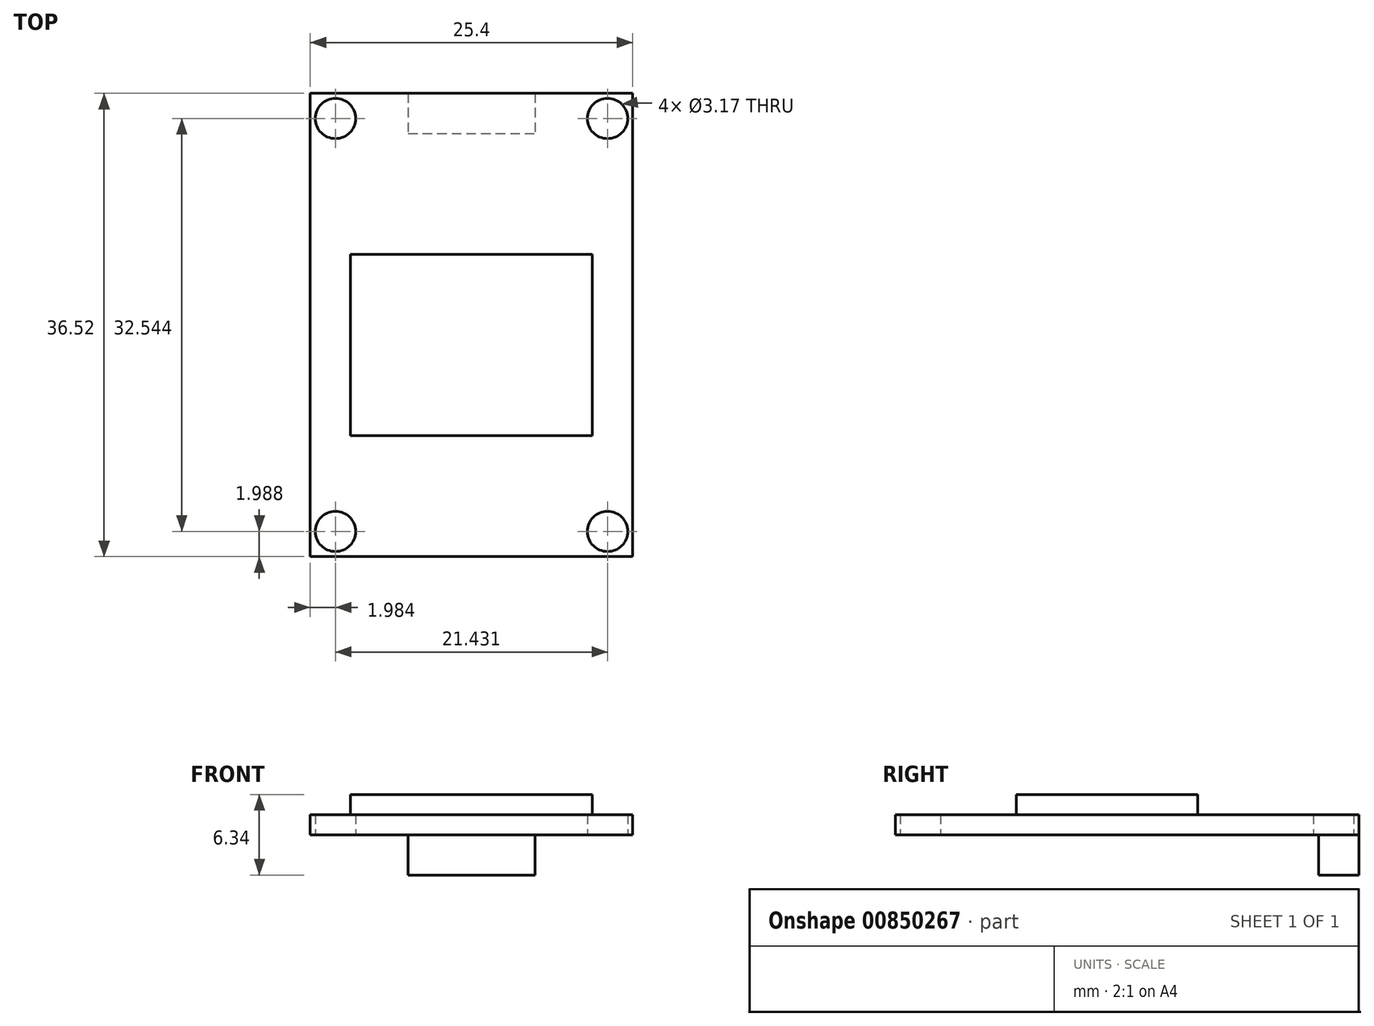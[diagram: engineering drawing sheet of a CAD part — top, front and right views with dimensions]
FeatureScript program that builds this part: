
annotation { "Feature Type Name" : "Feature", "Feature Type Description" : "" }
export const myFeature = defineFeature(function(context is Context, id is Id, definition is map)
    precondition{}
    {
        {
            var Q0;
            Q0=qCreatedBy(makeId("Top.planeOp"),FACE);
            var sketch = newSketch(context, id + "F0", { "sketchPlane" : qUnion([Q0])});
            skLineSegment(sketch, "E0.bottom", {"start": v(12.7, 18.26) * mm, "end": v(-12.7, 18.26) * mm});
            skLineSegment(sketch, "E0.top", {"start": v(12.7, -18.26) * mm, "end": v(-12.7, -18.26) * mm});
            skLineSegment(sketch, "E0.left", {"start": v(12.7, 18.26) * mm, "end": v(12.7, -18.26) * mm});
            skLineSegment(sketch, "E0.right", {"start": v(-12.7, 18.26) * mm, "end": v(-12.7, -18.26) * mm});
            skPoint(sketch, "E0.middle", {"position": v(0, 0) * mm});
            skCircle(sketch, "E1", {"center": v(-10.72, 16.27) * mm, "radius": 1.59 * mm});
            skCircle(sketch, "E2", {"center": v(10.72, 16.27) * mm, "radius": 1.59 * mm});
            skCircle(sketch, "E3", {"center": v(-10.72, -16.27) * mm, "radius": 1.59 * mm});
            skCircle(sketch, "E4", {"center": v(10.72, -16.27) * mm, "radius": 1.59 * mm});
            skLineSegment(sketch, "E5", {"start": v(-10.72, -16.27) * mm, "end": v(-10.72, 16.27) * mm, "construction": true});
            skLineSegment(sketch, "E6", {"start": v(-10.72, 16.27) * mm, "end": v(10.72, 16.27) * mm, "construction": true});
            skLineSegment(sketch, "E7", {"start": v(10.72, -16.27) * mm, "end": v(10.72, 16.27) * mm, "construction": true});
            skLineSegment(sketch, "E8", {"start": v(10.72, -16.27) * mm, "end": v(-10.72, -16.27) * mm, "construction": true});
            skSolve(sketch);
        }
        {
            var Q0;
            Q0=makeQuery(id+"F0.imprint","IMPRINT",FACE,{"disambiguationData":[TD([[makeQuery(id+"F0.imprint","IMPRINT",EDGE,{"derivedFrom":sQuery(id+"F0.wireOp",EDGE,"E0.bottom")}),1.0]])]});
            extrude(context, id + "F1", {"entities" : qUnion([Q0]), "depth" : 1.59 * mm, "offsetDistance" : 25.4 * mm});
        }
        {
            var Q0;
            Q0=makeQuery(id+"F1.opExtrude","CAP_FACE",FACE,{"disambiguationData":[OSD([sQuery(id+"F0.wireOp",EDGE,"E0.bottom"),sQuery(id+"F0.wireOp",EDGE,"E0.top"),sQuery(id+"F0.wireOp",EDGE,"E0.left"),sQuery(id+"F0.wireOp",EDGE,"E0.right"),sQuery(id+"F0.wireOp",EDGE,"E1"),sQuery(id+"F0.wireOp",EDGE,"E2"),sQuery(id+"F0.wireOp",EDGE,"E3"),sQuery(id+"F0.wireOp",EDGE,"E4")])],"isStart":false});
            var sketch = newSketch(context, id + "F2", { "sketchPlane" : qUnion([Q0])});
            skLineSegment(sketch, "E9.bottom", {"start": v(9.53, 5.56) * mm, "end": v(-9.53, 5.56) * mm});
            skLineSegment(sketch, "E9.top", {"start": v(9.53, -8.73) * mm, "end": v(-9.53, -8.73) * mm});
            skLineSegment(sketch, "E9.left", {"start": v(9.53, 5.56) * mm, "end": v(9.53, -8.73) * mm});
            skLineSegment(sketch, "E9.right", {"start": v(-9.53, 5.56) * mm, "end": v(-9.53, -8.73) * mm});
            skPoint(sketch, "E9.middle", {"position": v(0, -1.59) * mm});
            skSolve(sketch);
        }
        {
            var Q0;
            Q0=makeQuery(id+"F2.imprint","IMPRINT",FACE,{"disambiguationData":[TD([[makeQuery(id+"F2.imprint","IMPRINT",EDGE,{"derivedFrom":sQuery(id+"F2.wireOp",EDGE,"E9.bottom")}),1.0]])]});
            extrude(context, id + "F3", {"entities" : qUnion([Q0]), "operationType" : NewBodyOperationType.ADD, "depth" : 1.59 * mm, "offsetDistance" : 25.4 * mm});
        }
        {
            var Q0;
            Q0=makeQuery(id+"F1.opExtrude","CAP_FACE",FACE,{"disambiguationData":[OSD([sQuery(id+"F0.wireOp",EDGE,"E0.bottom"),sQuery(id+"F0.wireOp",EDGE,"E0.top"),sQuery(id+"F0.wireOp",EDGE,"E0.left"),sQuery(id+"F0.wireOp",EDGE,"E0.right"),sQuery(id+"F0.wireOp",EDGE,"E1"),sQuery(id+"F0.wireOp",EDGE,"E2"),sQuery(id+"F0.wireOp",EDGE,"E3"),sQuery(id+"F0.wireOp",EDGE,"E4")])],"isStart":true});
            var sketch = newSketch(context, id + "F4", { "sketchPlane" : qUnion([Q0])});
            skLineSegment(sketch, "E10.bottom", {"start": v(-5, -18.26) * mm, "end": v(5, -18.26) * mm});
            skLineSegment(sketch, "E10.top", {"start": v(-5, -15.08) * mm, "end": v(5, -15.08) * mm});
            skLineSegment(sketch, "E10.left", {"start": v(-5, -18.26) * mm, "end": v(-5, -15.08) * mm});
            skLineSegment(sketch, "E10.right", {"start": v(5, -18.26) * mm, "end": v(5, -15.08) * mm});
            skPoint(sketch, "E10.middle", {"position": v(0, -16.67) * mm});
            skSolve(sketch);
        }
        {
            var Q0;
            Q0=makeQuery(id+"F4.imprint","IMPRINT",FACE,{"disambiguationData":[TD([[makeQuery(id+"F4.imprint","IMPRINT",EDGE,{"derivedFrom":sQuery(id+"F4.wireOp",EDGE,"E10.bottom")}),-1.0]])]});
            extrude(context, id + "F5", {"entities" : qUnion([Q0]), "operationType" : NewBodyOperationType.ADD, "depth" : 3.17 * mm, "offsetDistance" : 25.4 * mm});
        }
    });
